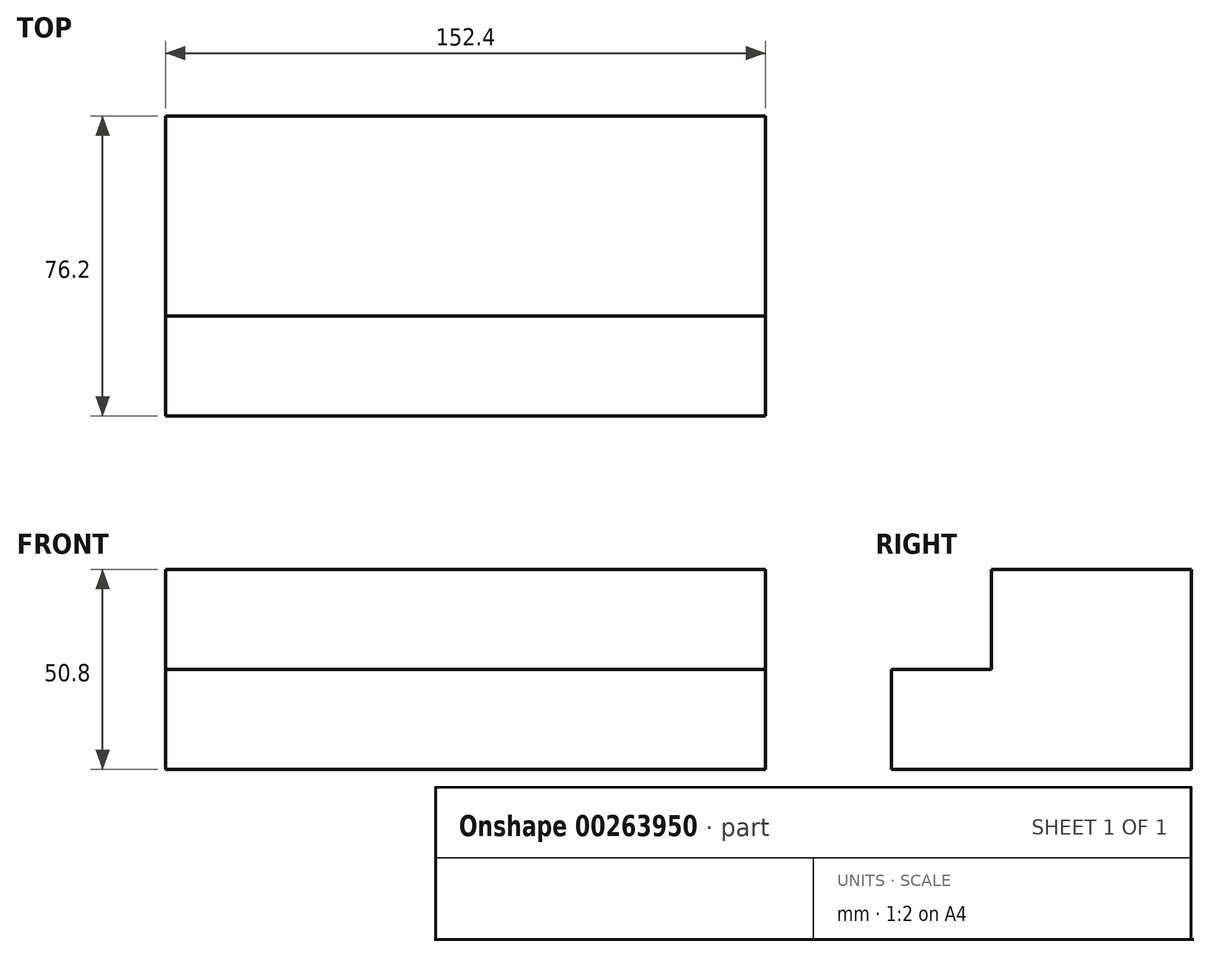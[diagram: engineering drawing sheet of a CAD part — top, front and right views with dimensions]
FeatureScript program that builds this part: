
annotation { "Feature Type Name" : "Feature", "Feature Type Description" : "" }
export const myFeature = defineFeature(function(context is Context, id is Id, definition is map)
    precondition{}
    {
        {
            var Q0;
            Q0=qCreatedBy(makeId("Right.planeOp"),FACE);
            var sketch = newSketch(context, id + "F0", { "sketchPlane" : qUnion([Q0])});
            skLineSegment(sketch, "E0", {"start": v(0, 0) * mm, "end": v(76.2, 0) * mm});
            skLineSegment(sketch, "E1", {"start": v(76.2, 0) * mm, "end": v(76.2, 50.8) * mm});
            skLineSegment(sketch, "E2", {"start": v(0, 0) * mm, "end": v(0, 25.4) * mm});
            skLineSegment(sketch, "E3", {"start": v(0, 25.4) * mm, "end": v(25.4, 25.4) * mm});
            skLineSegment(sketch, "E4", {"start": v(25.4, 25.4) * mm, "end": v(25.4, 50.8) * mm});
            skLineSegment(sketch, "E5", {"start": v(76.2, 50.8) * mm, "end": v(25.4, 50.8) * mm});
            skSolve(sketch);
        }
        {
            var Q0;
            Q0=makeQuery(id+"F0.imprint","IMPRINT",FACE,{"disambiguationData":[TD([[makeQuery(id+"F0.imprint","IMPRINT",EDGE,{"derivedFrom":sQuery(id+"F0.wireOp",EDGE,"E0")}),1.0]])]});
            extrude(context, id + "F1", {"entities" : qUnion([Q0]), "oppositeDirection" : true, "depth" : 152.4 * mm});
        }
    });
